# Revit family: door
name_source: partatom
category: Doors
revit_build: Autodesk Revit Architecture 2012 (Build: 20110309_2315(x64)
units: mm (PartAtom-declared; Revit-internal decimal feet)

## types (2) — shared parameters
Door Leaf Depth = 42 mm
Door Leaf Height = 2022 mm  [stored 6.63386 ft]
Frame Depth = 90 mm  [stored 0.295276 ft]
Frame Material = SAPine Frame - PAR - Varnished
Frame Projection Ext. = 25 mm  [stored 0.082021 ft]
Frame Projection Int. = 25 mm  [stored 0.082021 ft]
Frame Thickness = 69 mm
Frame Thickness minus Rebate = 29 mm
Frame Width = 44 mm  [stored 0.144357 ft]
Function = Interior
Glass Inset = None
Handle Height = 1100 mm  [stored 3.60892 ft]
Height = 2053 mm  [stored 6.73556 ft]
Leaf Material = SAPine Veneer - Solid Core - Varnished
Rebate Depth = 44 mm  [stored 0.144357 ft]
Rebate Width = 12 mm  [stored 0.0393701 ft]
Wall Closure = By host
Width = 805 mm  [stored 2.64108 ft]

## type names (no varying parameters)
- Door (Type 02)
- Door (Type 01)

note: [stored X ft] marks values corroborated as IEEE doubles in the binary element streams (Revit-internal decimal feet)

## geometry (parser evidence)
native form markers: Sweep x11
no freeform markers — native parametric forms only
